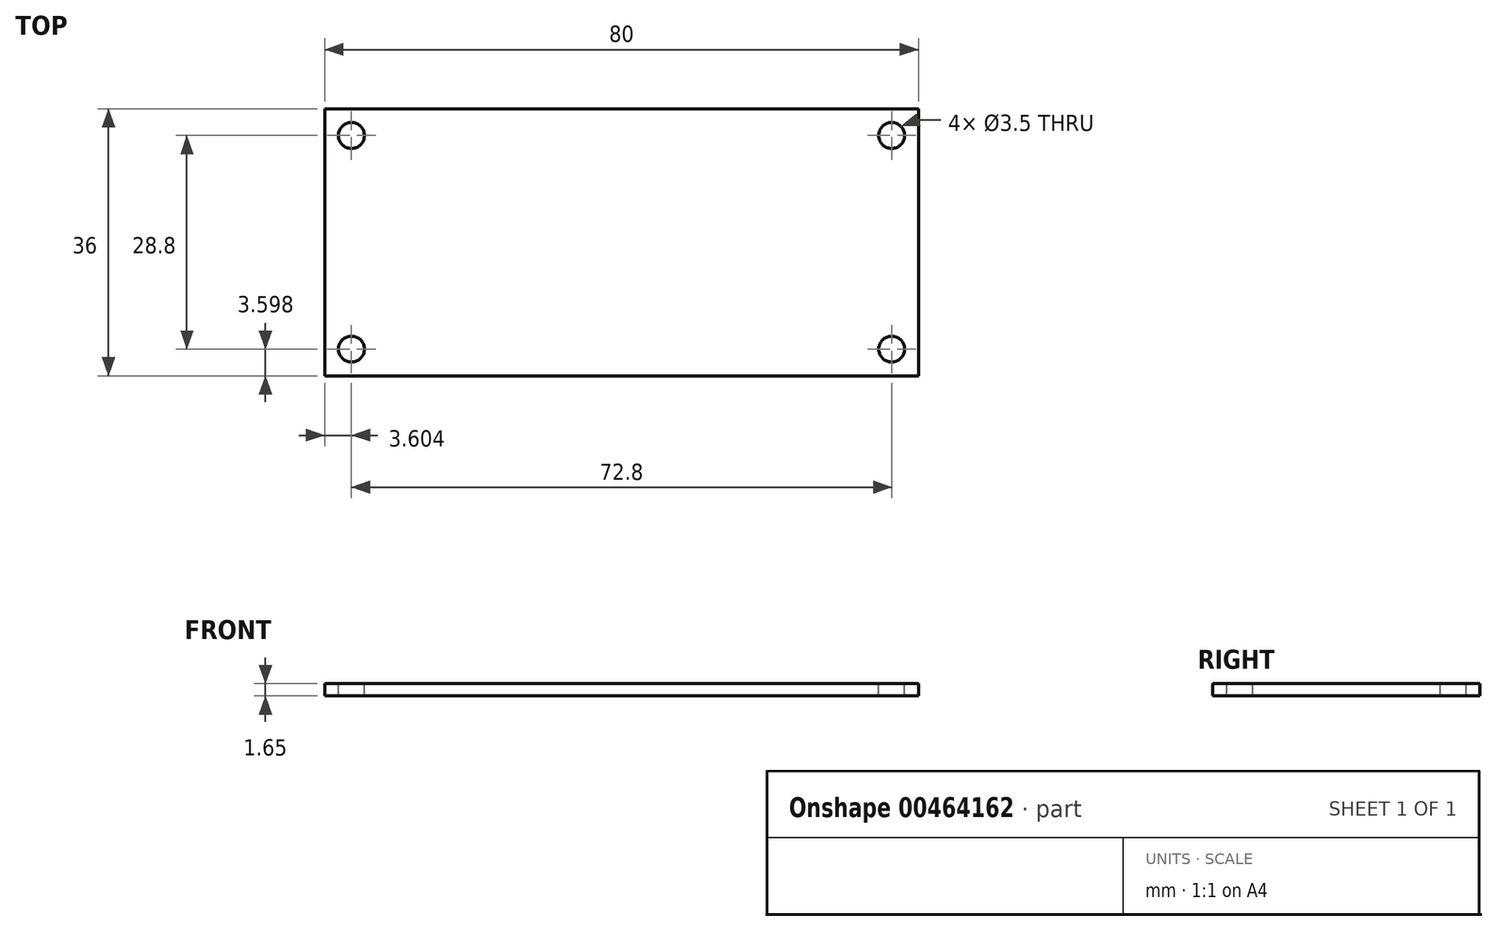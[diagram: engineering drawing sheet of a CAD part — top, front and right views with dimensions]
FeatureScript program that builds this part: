
annotation { "Feature Type Name" : "Feature", "Feature Type Description" : "" }
export const myFeature = defineFeature(function(context is Context, id is Id, definition is map)
    precondition{}
    {
        {
            var Q0;
            Q0=qCreatedBy(makeId("Top.planeOp"),FACE);
            var sketch = newSketch(context, id + "F0", { "sketchPlane" : qUnion([Q0])});
            skLineSegment(sketch, "E0.bottom", {"start": v(-69.47, 16.9) * mm, "end": v(10.53, 16.9) * mm});
            skLineSegment(sketch, "E0.top", {"start": v(-69.47, -19.1) * mm, "end": v(10.53, -19.1) * mm});
            skLineSegment(sketch, "E0.left", {"start": v(-69.47, 16.9) * mm, "end": v(-69.47, -19.1) * mm});
            skLineSegment(sketch, "E0.right", {"start": v(10.53, 16.9) * mm, "end": v(10.53, -19.1) * mm});
            skSolve(sketch);
        }
        {
            var Q0;
            Q0 = qSketchRegion(id + "F0", true);
            extrude(context, id + "F1", {"entities" : qUnion([Q0]), "depth" : 1.65 * mm, "offsetDistance" : 25 * mm});
        }
        {
            var Q0;
            Q0=makeQuery(id+"F1.opExtrude","CAP_FACE",FACE,{"disambiguationData":[OSD([sQuery(id+"F0.wireOp",EDGE,"E0.bottom"),sQuery(id+"F0.wireOp",EDGE,"E0.top"),sQuery(id+"F0.wireOp",EDGE,"E0.left"),sQuery(id+"F0.wireOp",EDGE,"E0.right")])],"isStart":false});
            var sketch = newSketch(context, id + "F2", { "sketchPlane" : qUnion([Q0])});
            skCircle(sketch, "E1", {"center": v(-65.87, 13.3) * mm, "radius": 1.75 * mm});
            skCircle(sketch, "E2", {"center": v(6.93, 13.3) * mm, "radius": 1.75 * mm});
            skCircle(sketch, "E3", {"center": v(6.93, -15.5) * mm, "radius": 1.75 * mm});
            skCircle(sketch, "E4", {"center": v(-65.87, -15.5) * mm, "radius": 1.75 * mm});
            skSolve(sketch);
        }
        {
            var Q0;
            Q0 = qSketchRegion(id + "F2", true);
            extrude(context, id + "F3", {"entities" : qUnion([Q0]), "operationType" : NewBodyOperationType.REMOVE, "oppositeDirection" : true, "depth" : 25 * mm});
        }
    });
